# Revit family: Albardilla MA escuadra (12-22).C-1
name_source: partatom
category: Modelos genéricos
units: mm (PartAtom-declared; Revit-internal decimal feet)

## family parameters
Compartido = No
Corte con vacíos al cargar = No
Cota de conector redondo = Diámetro de uso
Puede alojar armadura = No
Punto de cálculo de habitación = No
Se basa en plano de trabajo = No
Siempre vertical = No
Tipo de pieza = Normal

## types (5) — shared parameters
Altura = 44 mm  [stored 0.144357 ft]
Altura inferior = 29 mm
Ancho escuadra = 500 mm  [stored 1.64042 ft]
Descripción = Pieza de hormigón polímero con anclajes de acero inoxidable
Fabricante = ULMA Architectural Solutions
Material = Hormigón polímero STONEO. Color C-1
URL = https://www.ulmaarchitectural.com
dist = 15 mm  [stored 0.0492126 ft]
zero-valued in all types: Elevación por defecto

## per-type parameters (varying)
| type | Ancho | Ancho dos | Ancho dos dist. | Ancho total | Anclaje dos dist. ext. | Anclajes | Modelo |
| MA12E | 120 mm  [stored 0.393701 ft] | 85 mm  [stored 0.278871 ft] | 57 mm | 170 mm  [stored 0.557743 ft] | 43 mm | 85 mm  [stored 0.278871 ft] | Albardilla MA12 en escuadra |
| MA14E | 140 mm  [stored 0.459318 ft] | 95 mm  [stored 0.31168 ft] | 63 mm | 190 mm  [stored 0.62336 ft] | 48 mm | 95 mm  [stored 0.31168 ft] | Albardilla MA14 en escuadra |
| MA17E | 170 mm  [stored 0.557743 ft] | 110 mm  [stored 0.360892 ft] | 73 mm | 220 mm  [stored 0.721785 ft] | 55 mm  [stored 0.180446 ft] | 110 mm  [stored 0.360892 ft] | Albardilla MA17 en escuadra |
| MA19E | 190 mm  [stored 0.62336 ft] | 120 mm  [stored 0.393701 ft] | 80 mm  [stored 0.262467 ft] | 240 mm | 60 mm | 120 mm  [stored 0.393701 ft] | Albardilla MA19 en escuadra |
| MA22E | 220 mm  [stored 0.721785 ft] | 135 mm  [stored 0.442913 ft] | 90 mm  [stored 0.295276 ft] | 270 mm  [stored 0.885827 ft] | 68 mm | 135 mm  [stored 0.442913 ft] | Albardilla MA22 en escuadra |

note: column(s) folded — value = type name in every type: Código de montaje

note: [stored X ft] marks values corroborated as IEEE doubles in the binary element streams (Revit-internal decimal feet)
